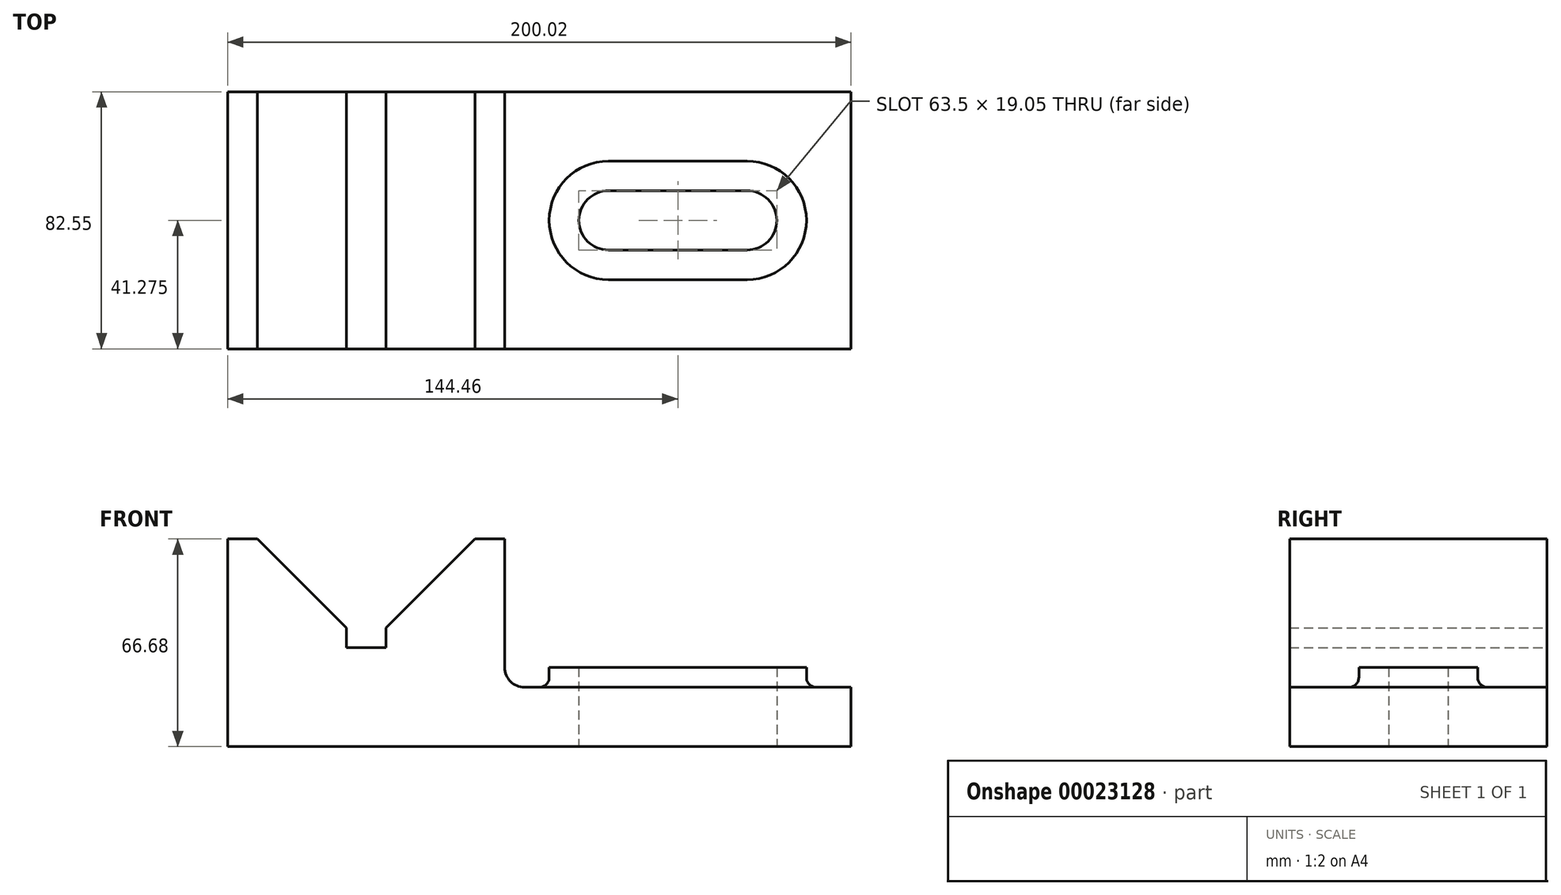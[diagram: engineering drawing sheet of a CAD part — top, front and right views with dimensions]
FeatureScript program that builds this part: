
annotation { "Feature Type Name" : "Feature", "Feature Type Description" : "" }
export const myFeature = defineFeature(function(context is Context, id is Id, definition is map)
    precondition{}
    {
        {
            var Q0;
            Q0=qCreatedBy(makeId("Front.planeOp"),FACE);
            var sketch = newSketch(context, id + "F0", { "sketchPlane" : qUnion([Q0])});
            skLineSegment(sketch, "E0.rect.bottom", {"start": v(-100.01, 33.34) * mm, "end": v(100.01, 33.34) * mm});
            skLineSegment(sketch, "E0.rect.top", {"start": v(-100.01, -33.34) * mm, "end": v(100.01, -33.34) * mm});
            skLineSegment(sketch, "E0.rect.left", {"start": v(-100.01, 33.34) * mm, "end": v(-100.01, -33.34) * mm});
            skLineSegment(sketch, "E0.rect.right", {"start": v(100.01, 33.34) * mm, "end": v(100.01, -33.34) * mm});
            skPoint(sketch, "E0.rect.middle", {"position": v(0, 0) * mm});
            skLineSegment(sketch, "E1", {"start": v(-90.49, 33.34) * mm, "end": v(-61.91, 4.76) * mm});
            skLineSegment(sketch, "E2", {"start": v(-20.64, 33.34) * mm, "end": v(-49.21, 4.76) * mm});
            skLineSegment(sketch, "E3.bottom", {"start": v(-61.91, 4.76) * mm, "end": v(-49.21, 4.76) * mm});
            skLineSegment(sketch, "E3.top", {"start": v(-61.91, -1.59) * mm, "end": v(-49.21, -1.59) * mm});
            skLineSegment(sketch, "E3.left", {"start": v(-61.91, 4.76) * mm, "end": v(-61.91, -1.59) * mm});
            skLineSegment(sketch, "E3.right", {"start": v(-49.21, 4.76) * mm, "end": v(-49.21, -1.59) * mm});
            skLineSegment(sketch, "E4.bottom", {"start": v(-11.11, 33.34) * mm, "end": v(100.01, 33.34) * mm});
            skLineSegment(sketch, "E4.top", {"start": v(-4.76, -14.29) * mm, "end": v(100.01, -14.29) * mm});
            skLineSegment(sketch, "E4.left", {"start": v(-11.11, 33.34) * mm, "end": v(-11.11, -7.94) * mm});
            skLineSegment(sketch, "E4.right", {"start": v(100.01, 33.34) * mm, "end": v(100.01, -14.29) * mm});
            skPoint(sketch, "E5.visualSharp", {"position": v(-11.11, -14.29) * mm});
            skArc(sketch, "E5.filletArc", {"start": v(-11.11, -7.94) * mm, "mid": v(-9.25, -12.43) * mm, "end": v(-4.76, -14.29) * mm});
            skSolve(sketch);
        }
        {
            var Q0;
            Q0=makeQuery(id+"F0.imprint","IMPRINT",FACE,{"disambiguationData":[TD([[makeQuery(id+"F0.imprint","IMPRINT",EDGE,{"derivedFrom":sQuery(id+"F0.wireOp",EDGE,"E0.rect.top")}),1.0]])]});
            extrude(context, id + "F1", {"entities" : qUnion([Q0]), "depth" : 82.55 * mm});
        }
        {
            var Q0;
            Q0=makeQuery(id+"F1.opExtrude","SWEPT_FACE",FACE,{"disambiguationData":[OSD([sQuery(id+"F0.wireOp",EDGE,"E4.top")])]});
            var sketch = newSketch(context, id + "F2", { "sketchPlane" : qUnion([Q0])});
            skLineSegment(sketch, "E6.bottom", {"start": v(22.23, -50.8) * mm, "end": v(66.67, -50.8) * mm});
            skLineSegment(sketch, "E6.top", {"start": v(22.23, -31.75) * mm, "end": v(66.67, -31.75) * mm});
            skLineSegment(sketch, "E6.left", {"start": v(22.23, -50.8) * mm, "end": v(22.23, -31.75) * mm});
            skLineSegment(sketch, "E6.right", {"start": v(66.67, -50.8) * mm, "end": v(66.67, -31.75) * mm});
            skLineSegment(sketch, "E7", {"start": v(66.67, -31.75) * mm, "end": v(66.67, 0) * mm});
            skLineSegment(sketch, "E8", {"start": v(66.67, -50.8) * mm, "end": v(66.67, -82.55) * mm});
            skLineSegment(sketch, "E9", {"start": v(66.67, -31.75) * mm, "end": v(100.01, -31.75) * mm});
            skArc(sketch, "E10", {"start": v(22.22, -31.75) * mm, "mid": v(12.7, -41.28) * mm, "end": v(22.22, -50.8) * mm});
            skArc(sketch, "E11", {"start": v(66.67, -50.8) * mm, "mid": v(76.2, -41.28) * mm, "end": v(66.67, -31.75) * mm});
            skLineSegment(sketch, "E12.bottom", {"start": v(22.23, -60.33) * mm, "end": v(66.67, -60.33) * mm});
            skLineSegment(sketch, "E12.top", {"start": v(22.23, -22.23) * mm, "end": v(66.67, -22.23) * mm});
            skLineSegment(sketch, "E12.left", {"start": v(22.23, -60.33) * mm, "end": v(22.23, -22.23) * mm});
            skLineSegment(sketch, "E12.right", {"start": v(66.67, -60.33) * mm, "end": v(66.67, -22.23) * mm});
            skArc(sketch, "E13", {"start": v(66.67, -60.33) * mm, "mid": v(85.72, -41.28) * mm, "end": v(66.67, -22.23) * mm});
            skArc(sketch, "E14", {"start": v(22.22, -22.23) * mm, "mid": v(3.18, -41.28) * mm, "end": v(22.23, -60.33) * mm});
            skLineSegment(sketch, "E15", {"start": v(-11.11, 0) * mm, "end": v(-11.11, -89.29) * mm});
            skLineSegment(sketch, "E16", {"start": v(-11.11, -89.29) * mm, "end": v(-11.11, 0) * mm});
            skLineSegment(sketch, "E17", {"start": v(22.23, -31.75) * mm, "end": v(-11.11, -31.75) * mm});
            skSolve(sketch);
        }
        {
            var Q0;
            {var subQ5=sQuery(id+"F2.wireOp",EDGE,"E10");Q0=makeQuery(id+"F2.imprint","IMPRINT",FACE,{"disambiguationData":[TD([[makeQuery(id+"F2.imprint","IMPRINT",EDGE,{"derivedFrom":subQ5}),-1.0]])]});}
            var Q1;
            {var subQ0=sQuery(id+"F2.wireOp",EDGE,"E13");var subQ1=sQuery(id+"F2.wireOp",EDGE,"E9");var subQ2=makeQuery(id+"F2.imprint","INTERSECT",VERTEX,{"derivedFrom":[subQ1,subQ0]});Q1=makeQuery(id+"F2.imprint","IMPRINT",FACE,{"disambiguationData":[TD([[makeQuery(id+"F2.imprint","IMPRINT",EDGE,{"disambiguationData":[TD([[subQ2,1.0]])],"derivedFrom":subQ1}),1.0]])]});}
            var Q2;
            {var subQ5=sQuery(id+"F2.wireOp",EDGE,"E11");Q2=makeQuery(id+"F2.imprint","IMPRINT",FACE,{"disambiguationData":[TD([[makeQuery(id+"F2.imprint","IMPRINT",EDGE,{"derivedFrom":subQ5}),-1.0]])]});}
            var Q3;
            {var subQ2=sQuery(id+"F2.wireOp",EDGE,"E6.bottom");Q3=makeQuery(id+"F2.imprint","IMPRINT",FACE,{"disambiguationData":[TD([[makeQuery(id+"F2.imprint","IMPRINT",EDGE,{"derivedFrom":subQ2}),-1.0]])]});}
            var Q4;
            {var subQ2=sQuery(id+"F2.wireOp",EDGE,"E6.top");Q4=makeQuery(id+"F2.imprint","IMPRINT",FACE,{"disambiguationData":[TD([[makeQuery(id+"F2.imprint","IMPRINT",EDGE,{"derivedFrom":subQ2}),1.0]])]});}
            var Q5;
            {var subQ0=sQuery(id+"F2.wireOp",EDGE,"E14");var subQ1=sQuery(id+"F2.wireOp",EDGE,"2dfc0fac-0252-4003-b473-88085082771b");var subQ2=makeQuery(id+"F2.imprint","INTERSECT",VERTEX,{"derivedFrom":[subQ1,subQ0]});Q5=makeQuery(id+"F2.imprint","IMPRINT",FACE,{"disambiguationData":[TD([[makeQuery(id+"F2.imprint","IMPRINT",EDGE,{"disambiguationData":[TD([[subQ2,1.0]])],"derivedFrom":subQ0}),1.0]])]});}
            extrude(context, id + "F3", {"entities" : qUnion([Q0, Q1, Q2, Q3, Q4, Q5]), "operationType" : NewBodyOperationType.ADD, "depth" : 6.35 * mm});
        }
        {
            var Q0;
            Q0=makeQuery(id+"F3.opExtrude","CAP_EDGE",EDGE,{"disambiguationData":[OSD([sQuery(id+"F2.wireOp",EDGE,"E14")])],"isStart":true});
            var Q1;
            Q1=makeQuery(id+"F3.opExtrude","CAP_EDGE",EDGE,{"disambiguationData":[OSD([sQuery(id+"F2.wireOp",EDGE,"E12.bottom")])],"isStart":true});
            var Q2;
            Q2=makeQuery(id+"F3.opExtrude","CAP_EDGE",EDGE,{"disambiguationData":[OSD([sQuery(id+"F2.wireOp",EDGE,"E13")])],"isStart":true});
            var Q3;
            Q3=makeQuery(id+"F3.opExtrude","CAP_EDGE",EDGE,{"disambiguationData":[OSD([sQuery(id+"F2.wireOp",EDGE,"E12.top")])],"isStart":true});
            fillet(context, id + "F4", {"entities" : qUnion([Q0, Q1, Q2, Q3]), "radius" : 3.17 * mm, "tangentPropagation" : true, "allowEdgeOverflow" : false});
        }
        {
            var Q0;
            Q0=makeQuery(id+"F3.boolean.opBoolean","SPLIT",FACE,{"disambiguationData":[TD([makeQuery(id+"F3.opExtrude","SWEPT_FACE",FACE,{"disambiguationData":[OSD([sQuery(id+"F2.wireOp",EDGE,"E6.bottom")])]})])],"derivedFrom":makeQuery(id+"F1.opExtrude","SWEPT_FACE",FACE,{"disambiguationData":[OSD([sQuery(id+"F0.wireOp",EDGE,"E4.top")])]})});
            extrude(context, id + "F5", {"entities" : qUnion([Q0]), "operationType" : NewBodyOperationType.REMOVE, "oppositeDirection" : true, "depth" : 25.4 * mm});
        }
    });
